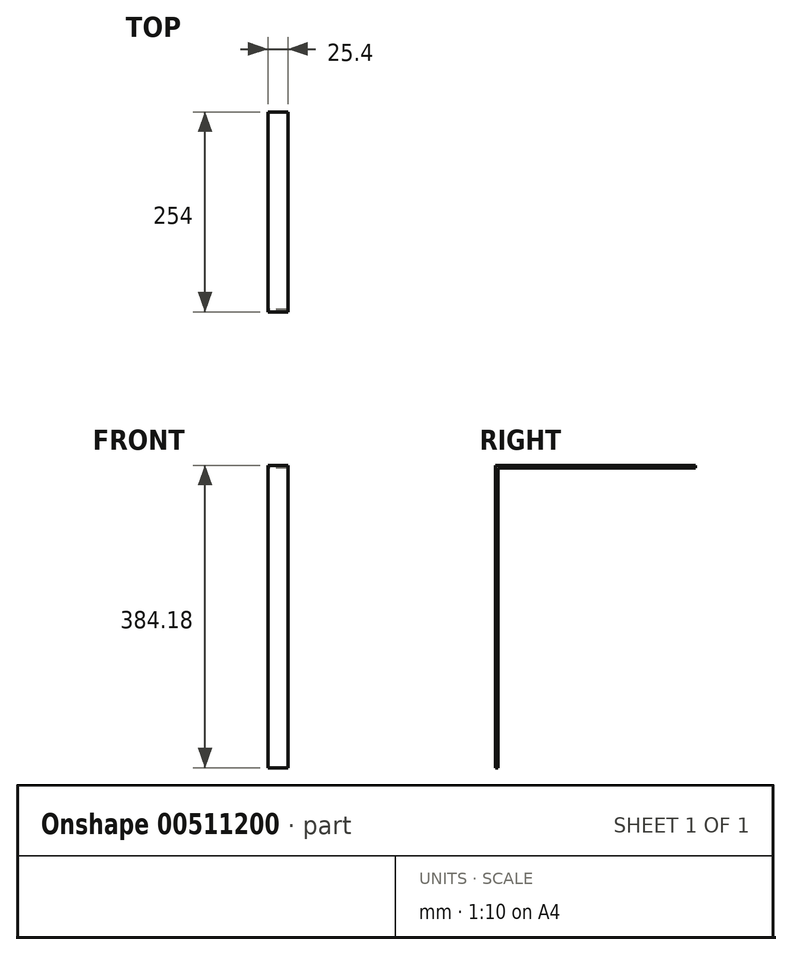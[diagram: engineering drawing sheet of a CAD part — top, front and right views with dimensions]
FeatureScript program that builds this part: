
annotation { "Feature Type Name" : "Feature", "Feature Type Description" : "" }
export const myFeature = defineFeature(function(context is Context, id is Id, definition is map)
    precondition{}
    {
        {
            var Q0;
            Q0=qCreatedBy(makeId("Right.planeOp"),FACE);
            var sketch = newSketch(context, id + "F0", { "sketchPlane" : qUnion([Q0])});
            skLineSegment(sketch, "E0", {"start": v(0, 0) * mm, "end": v(0, -381) * mm});
            skLineSegment(sketch, "E1", {"start": v(0, -381) * mm, "end": v(-3.17, -381) * mm});
            skLineSegment(sketch, "E2", {"start": v(-3.17, -381) * mm, "end": v(-3.17, 3.18) * mm});
            skLineSegment(sketch, "E3", {"start": v(-3.17, 3.17) * mm, "end": v(250.83, 3.17) * mm});
            skLineSegment(sketch, "E4", {"start": v(250.83, 3.18) * mm, "end": v(250.83, 0) * mm});
            skLineSegment(sketch, "E5", {"start": v(250.83, 0) * mm, "end": v(0, 0) * mm});
            skSolve(sketch);
        }
        {
            var Q0;
            Q0 = qSketchRegion(id + "F0", true);
            extrude(context, id + "F1", {"entities" : qUnion([Q0]), "endBound" : BoundingType.SYMMETRIC, "depth" : 25.4 * mm});
        }
    });
